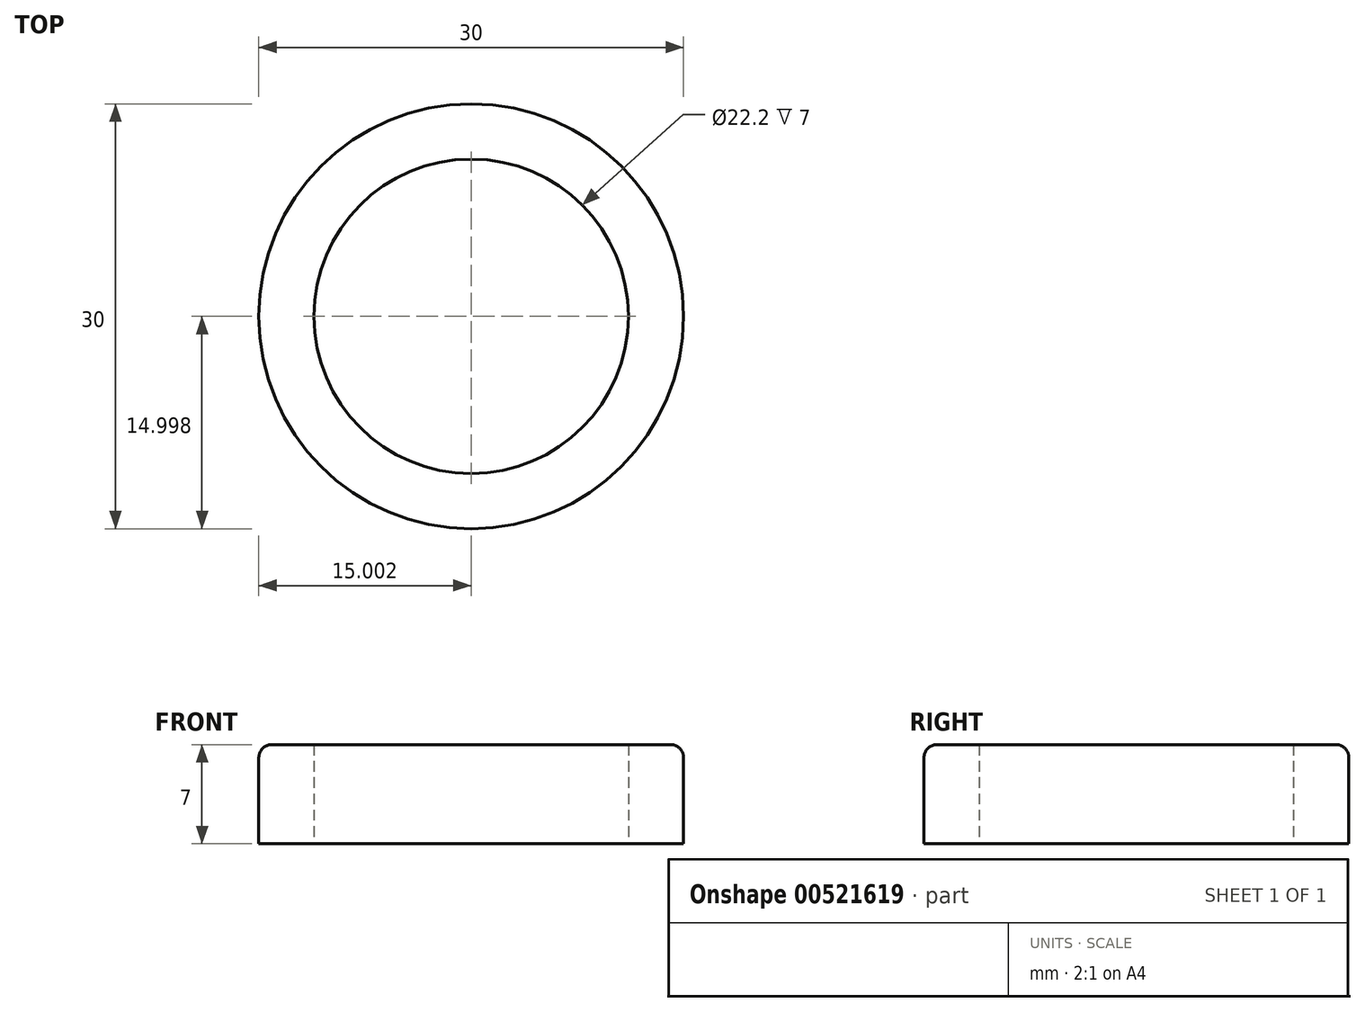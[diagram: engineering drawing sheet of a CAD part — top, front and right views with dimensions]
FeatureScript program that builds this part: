
annotation { "Feature Type Name" : "Feature", "Feature Type Description" : "" }
export const myFeature = defineFeature(function(context is Context, id is Id, definition is map)
    precondition{}
    {
        {
            var Q0;
            Q0=qCreatedBy(makeId("Top.planeOp"),FACE);
            var sketch = newSketch(context, id + "F0", { "sketchPlane" : qUnion([Q0])});
            skCircle(sketch, "E0", {"center": v(-8.18, 3.3) * mm, "radius": 11.1 * mm});
            skCircle(sketch, "E1", {"center": v(-8.18, 3.3) * mm, "radius": 15 * mm});
            skSolve(sketch);
        }
        {
            var Q0;
            Q0=makeQuery(id+"F0.imprint","IMPRINT",FACE,{"disambiguationData":[TD([[makeQuery(id+"F0.imprint","IMPRINT",EDGE,{"derivedFrom":sQuery(id+"F0.wireOp",EDGE,"E0")}),-1.0]])]});
            extrude(context, id + "F1", {"entities" : qUnion([Q0]), "depth" : 7 * mm, "offsetDistance" : 25 * mm});
        }
        {
            var Q0;
            Q0=makeQuery(id+"F1.opExtrude","CAP_EDGE",EDGE,{"disambiguationData":[OSD([sQuery(id+"F0.wireOp",EDGE,"E1")])],"isStart":false});
            fillet(context, id + "F2", {"entities" : qUnion([Q0]), "radius" : .9 * mm, "tangentPropagation" : true, "allowEdgeOverflow" : false});
        }
    });
